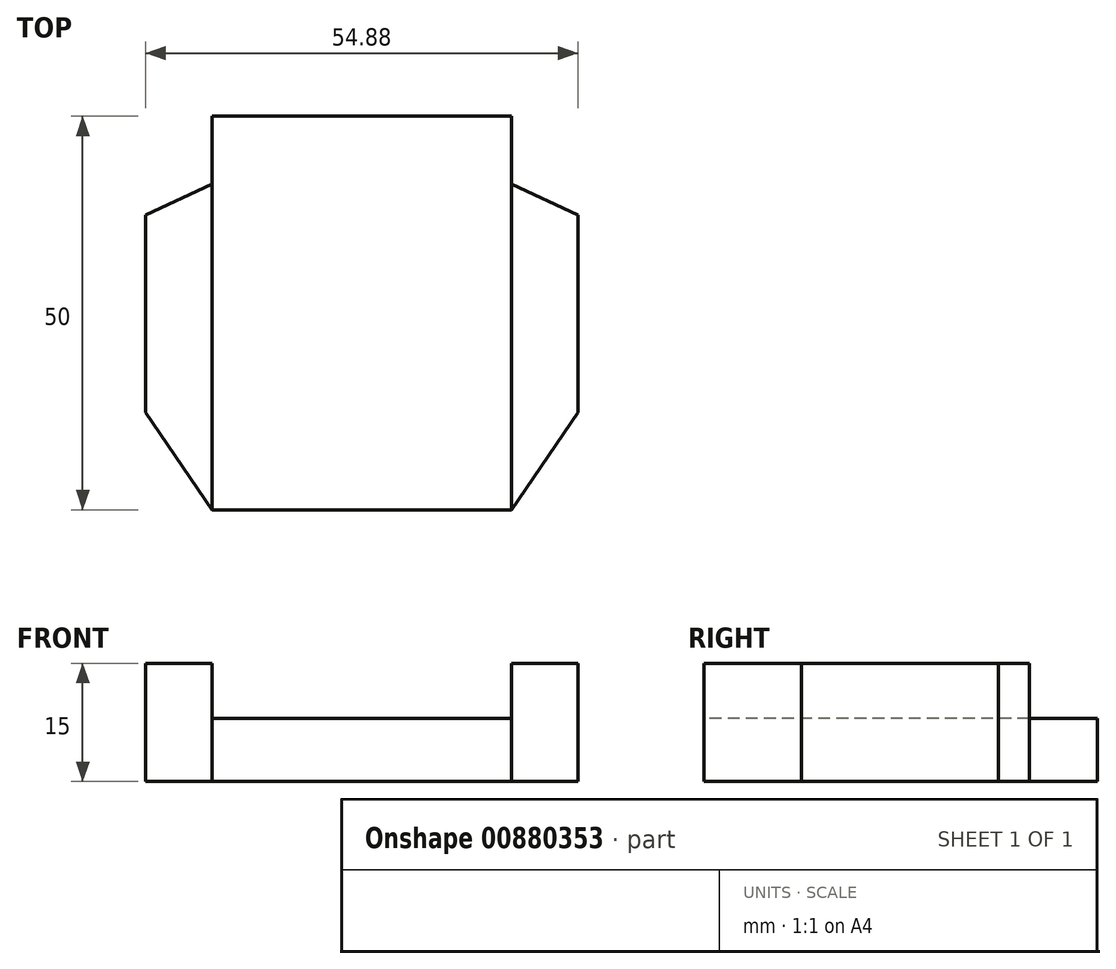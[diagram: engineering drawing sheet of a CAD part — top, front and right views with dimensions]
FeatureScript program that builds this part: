
annotation { "Feature Type Name" : "Feature", "Feature Type Description" : "" }
export const myFeature = defineFeature(function(context is Context, id is Id, definition is map)
    precondition{}
    {
        {
            var Q0;
            Q0=qCreatedBy(makeId("Top.planeOp"),FACE);
            var sketch = newSketch(context, id + "F0", { "sketchPlane" : qUnion([Q0])});
            skLineSegment(sketch, "E0.bottom", {"start": v(-55.3, 14.02) * mm, "end": v(-17.3, 14.02) * mm});
            skLineSegment(sketch, "E0.top", {"start": v(-55.3, -35.98) * mm, "end": v(-17.3, -35.98) * mm});
            skLineSegment(sketch, "E0.left", {"start": v(-55.3, 14.02) * mm, "end": v(-55.3, -35.98) * mm});
            skLineSegment(sketch, "E0.right", {"start": v(-17.3, 14.02) * mm, "end": v(-17.3, -35.98) * mm});
            skLineSegment(sketch, "E1", {"start": v(-55.3, -35.98) * mm, "end": v(-63.74, -23.6) * mm});
            skLineSegment(sketch, "E2", {"start": v(-63.74, -23.6) * mm, "end": v(-63.74, 1.44) * mm});
            skLineSegment(sketch, "E3", {"start": v(-63.74, 1.44) * mm, "end": v(-55.3, 5.37) * mm});
            skLineSegment(sketch, "E4", {"start": v(-36.3, 14.02) * mm, "end": v(-36.3, -35.98) * mm, "construction": true});
            skLineSegment(sketch, "E5.MirrorCS", {"start": v(-8.86, 1.44) * mm, "end": v(-17.3, 5.37) * mm});
            skLineSegment(sketch, "E6.MirrorCS", {"start": v(-8.86, -23.6) * mm, "end": v(-8.86, 1.44) * mm});
            skLineSegment(sketch, "E7.MirrorCS", {"start": v(-17.3, -35.98) * mm, "end": v(-8.86, -23.6) * mm});
            skSolve(sketch);
        }
        {
            var Q0;
            {var subQ3=sQuery(id+"F0.wireOp",EDGE,"E0.bottom");Q0=makeQuery(id+"F0.imprint","IMPRINT",FACE,{"disambiguationData":[TD([[makeQuery(id+"F0.imprint","IMPRINT",EDGE,{"derivedFrom":subQ3}),-1.0]])]});}
            extrude(context, id + "F1", {"entities" : qUnion([Q0]), "depth" : 8 * mm, "offsetDistance" : 25 * mm});
        }
        {
            var Q0;
            {var subQ2=sQuery(id+"F0.wireOp",EDGE,"E5.MirrorCS");Q0=makeQuery(id+"F0.imprint","IMPRINT",FACE,{"disambiguationData":[TD([[makeQuery(id+"F0.imprint","IMPRINT",EDGE,{"derivedFrom":subQ2}),1.0]])]});}
            var Q1;
            {var subQ0=sQuery(id+"F0.wireOp",EDGE,"E1");Q1=makeQuery(id+"F0.imprint","IMPRINT",FACE,{"disambiguationData":[TD([[makeQuery(id+"F0.imprint","IMPRINT",EDGE,{"derivedFrom":subQ0}),-1.0]])]});}
            extrude(context, id + "F2", {"entities" : qUnion([Q0, Q1]), "operationType" : NewBodyOperationType.ADD, "depth" : 15 * mm, "offsetDistance" : 25 * mm});
        }
    });
